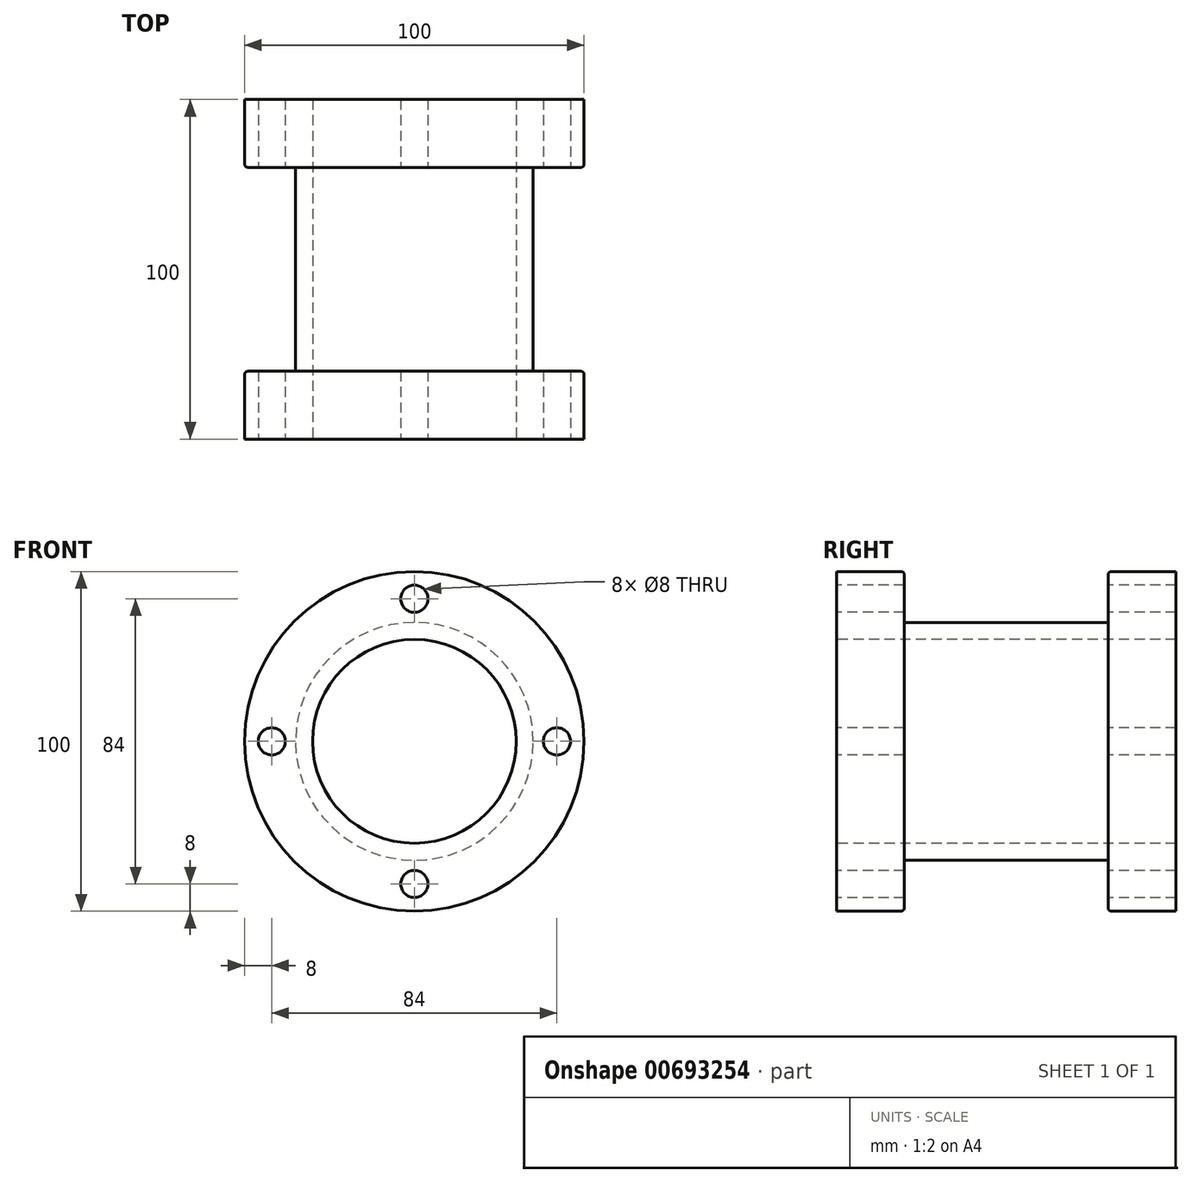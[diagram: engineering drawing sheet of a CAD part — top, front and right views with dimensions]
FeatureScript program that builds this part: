
annotation { "Feature Type Name" : "Feature", "Feature Type Description" : "" }
export const myFeature = defineFeature(function(context is Context, id is Id, definition is map)
    precondition{}
    {
        {
            var Q0;
            Q0=qCreatedBy(makeId("Front.planeOp"),FACE);
            var sketch = newSketch(context, id + "F0", { "sketchPlane" : qUnion([Q0])});
            skCircle(sketch, "E0", {"center": v(0, 0) * mm, "radius": 35 * mm});
            skSolve(sketch);
        }
        {
            var Q0;
            Q0=makeQuery(id+"F0.imprint","IMPRINT",FACE,{"disambiguationData":[TD([[makeQuery(id+"F0.imprint","IMPRINT",EDGE,{"derivedFrom":sQuery(id+"F0.wireOp",EDGE,"E0")}),1.0]])]});
            extrude(context, id + "F1", {"entities" : qUnion([Q0]), "endBound" : BoundingType.SYMMETRIC, "depth" : 60 * mm, "offsetDistance" : 25 * mm});
        }
        {
            var Q0;
            Q0=qCreatedBy(makeId("Front.planeOp"),FACE);
            cPlane(context, id + "F2", {"entities" : qUnion([Q0]), "cplaneType" : CPlaneType.OFFSET, "offset" : 30 * mm, "width" : 150 * mm, "height" : 150 * mm});
        }
        {
            var Q0;
            Q0=qCreatedBy(id+"F2.planeOp",FACE);
            var sketch = newSketch(context, id + "F3", { "sketchPlane" : qUnion([Q0])});
            skCircle(sketch, "E1", {"center": v(0, 0) * mm, "radius": 50 * mm});
            skSolve(sketch);
        }
        {
            var Q0;
            Q0=makeQuery(id+"F3.imprint","IMPRINT",FACE,{"disambiguationData":[TD([[makeQuery(id+"F3.imprint","IMPRINT",EDGE,{"derivedFrom":sQuery(id+"F3.wireOp",EDGE,"E1")}),1.0]])]});
            extrude(context, id + "F4", {"entities" : qUnion([Q0]), "operationType" : NewBodyOperationType.ADD, "depth" : 20 * mm, "offsetDistance" : 25 * mm});
        }
        {
            var Q0;
            Q0=qCreatedBy(makeId("Front.planeOp"),FACE);
            cPlane(context, id + "F5", {"entities" : qUnion([Q0]), "cplaneType" : CPlaneType.OFFSET, "offset" : 30 * mm, "oppositeDirection" : true, "width" : 150 * mm, "height" : 150 * mm});
        }
        {
            var Q0;
            Q0=qCreatedBy(id+"F5.planeOp",FACE);
            var sketch = newSketch(context, id + "F6", { "sketchPlane" : qUnion([Q0])});
            skCircle(sketch, "E2", {"center": v(0, 0) * mm, "radius": 50 * mm});
            skSolve(sketch);
        }
        {
            var Q0;
            Q0 = qSketchRegion(id + "F6", true);
            extrude(context, id + "F7", {"entities" : qUnion([Q0]), "operationType" : NewBodyOperationType.ADD, "oppositeDirection" : true, "depth" : 20 * mm, "offsetDistance" : 25 * mm});
        }
        {
            var Q0;
            Q0=makeQuery(id+"F4.opExtrude","CAP_FACE",FACE,{"disambiguationData":[OSD([sQuery(id+"F3.wireOp",EDGE,"E1")])],"isStart":false});
            var sketch = newSketch(context, id + "F8", { "sketchPlane" : qUnion([Q0])});
            skCircle(sketch, "E3", {"center": v(0, 0) * mm, "radius": 30 * mm});
            skSolve(sketch);
        }
        {
            var Q0;
            Q0=sQuery(id+"F8.wireOp",VERTEX,"E3.center");
            var Q1;
            Q1=makeQuery(id+"F1.opExtrude","SWEPT_BODY",BODY,{"disambiguationData":[OSD([sQuery(id+"F0.wireOp",EDGE,"E0")])]});
            hole(context, id + "F9", {"style" : HoleStyle.SIMPLE, "endStyle" : HoleEndStyle.THROUGH, "holeDiameter" : 60 * mm, "majorDiameter" : 5 * mm, "isTappedThrough" : true, "tappedDepth" : 12 * mm, "tapClearance" : 3, "locations" : qUnion([Q0]), "scope" : qUnion([Q1])});
        }
        {
            var Q0;
            Q0=makeQuery(id+"F4.opExtrude","CAP_FACE",FACE,{"disambiguationData":[OSD([sQuery(id+"F3.wireOp",EDGE,"E1")])],"isStart":false});
            var sketch = newSketch(context, id + "F10", { "sketchPlane" : qUnion([Q0])});
            skLineSegment(sketch, "E4", {"start": v(0, 50) * mm, "end": v(0, 42) * mm});
            skCircle(sketch, "E5", {"center": v(0, 42) * mm, "radius": 4 * mm});
            skCircle(sketch, "E6.MirrorC", {"center": v(0, -42) * mm, "radius": 4 * mm});
            skLineSegment(sketch, "E7", {"start": v(-50, 0) * mm, "end": v(-42, 0) * mm});
            skCircle(sketch, "E8", {"center": v(-42, 0) * mm, "radius": 4 * mm});
            skCircle(sketch, "E9.MirrorC", {"center": v(42, 0) * mm, "radius": 4 * mm});
            skSolve(sketch);
        }
        {
            var Q0;
            Q0=sQuery(id+"F10.wireOp",VERTEX,"E4.end");
            var Q1;
            Q1=sQuery(id+"F10.wireOp",VERTEX,"E7.end");
            var Q2;
            Q2=sQuery(id+"F10.wireOp",VERTEX,"E6.MirrorC.center");
            var Q3;
            Q3=sQuery(id+"F10.wireOp",VERTEX,"E9.MirrorC.center");
            var Q4;
            Q4=makeQuery(id+"F1.opExtrude","SWEPT_BODY",BODY,{"disambiguationData":[OSD([sQuery(id+"F0.wireOp",EDGE,"E0")])]});
            hole(context, id + "F11", {"style" : HoleStyle.SIMPLE, "endStyle" : HoleEndStyle.THROUGH, "holeDiameter" : 8 * mm, "majorDiameter" : 5 * mm, "isTappedThrough" : true, "tappedDepth" : 12 * mm, "tapClearance" : 3, "locations" : qUnion([Q0, Q1, Q2, Q3]), "scope" : qUnion([Q4])});
        }
        {
            var Q0;
            Q0=makeQuery(id+"F1.opExtrude","CAP_EDGE",EDGE,{"disambiguationData":[OSD([sQuery(id+"F0.wireOp",EDGE,"E0")])],"isStart":false});
            var Q1;
            Q1=makeQuery(id+"F1.opExtrude","CAP_EDGE",EDGE,{"disambiguationData":[OSD([sQuery(id+"F0.wireOp",EDGE,"E0")])],"isStart":true});
            var Q2;
            Q2=makeQuery(id+"F7.opExtrude","CAP_EDGE",EDGE,{"disambiguationData":[OSD([sQuery(id+"F6.wireOp",EDGE,"E2")])],"isStart":true});
            var Q3;
            Q3=makeQuery(id+"F4.opExtrude","CAP_EDGE",EDGE,{"disambiguationData":[OSD([sQuery(id+"F3.wireOp",EDGE,"E1")])],"isStart":true});
            fillet(context, id + "F12", {"entities" : qUnion([Q0, Q1, Q2, Q3]), "radius" : 1 * mm, "tangentPropagation" : true, "allowEdgeOverflow" : false});
        }
    });
